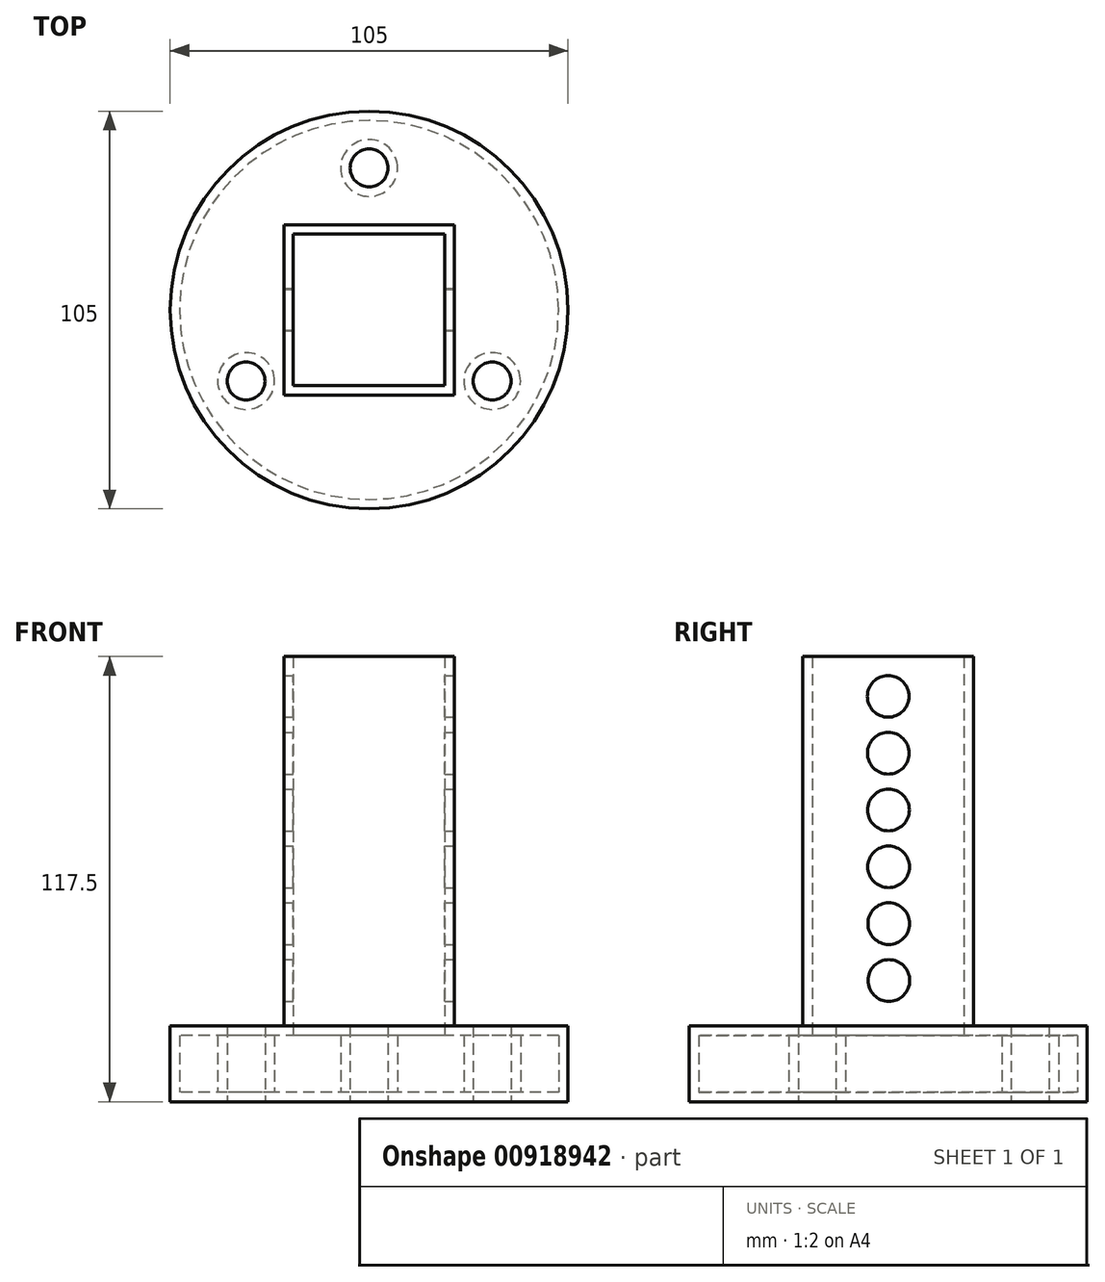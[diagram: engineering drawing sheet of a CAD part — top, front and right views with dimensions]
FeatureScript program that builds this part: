
annotation { "Feature Type Name" : "Feature", "Feature Type Description" : "" }
export const myFeature = defineFeature(function(context is Context, id is Id, definition is map)
    precondition{}
    {
        {
            var Q0;
            Q0=qCreatedBy(makeId("Top.planeOp"),FACE);
            var sketch = newSketch(context, id + "F0", { "sketchPlane" : qUnion([Q0])});
            skCircle(sketch, "E0", {"center": v(0, 0) * mm, "radius": 50 * mm});
            skCircle(sketch, "E1", {"center": v(0, 37.5) * mm, "radius": 7.5 * mm});
            skCircle(sketch, "E2.1.0", {"center": v(-32.48, -18.75) * mm, "radius": 7.5 * mm});
            skCircle(sketch, "E2.2.0", {"center": v(32.48, -18.75) * mm, "radius": 7.5 * mm});
            skSolve(sketch);
        }
        {
            var Q0;
            Q0=makeQuery(id+"F0.imprint","IMPRINT",FACE,{"disambiguationData":[TD([[makeQuery(id+"F0.imprint","IMPRINT",EDGE,{"derivedFrom":sQuery(id+"F0.wireOp",EDGE,"E0")}),1.0]])]});
            extrude(context, id + "F1", {"entities" : qUnion([Q0]), "depth" : 15 * mm, "offsetDistance" : 25 * mm});
        }
        {
            var Q0;
            Q0=makeQuery(id+"F1.opExtrude","CAP_FACE",FACE,{"disambiguationData":[OSD([sQuery(id+"F0.wireOp",EDGE,"E0"),sQuery(id+"F0.wireOp",EDGE,"E1"),sQuery(id+"F0.wireOp",EDGE,"E2.1.0"),sQuery(id+"F0.wireOp",EDGE,"E2.2.0")])],"isStart":false});
            var sketch = newSketch(context, id + "F2", { "sketchPlane" : qUnion([Q0])});
            skLineSegment(sketch, "E3.bottom", {"start": v(20, 20) * mm, "end": v(-20, 20) * mm});
            skLineSegment(sketch, "E3.top", {"start": v(20, -20) * mm, "end": v(-20, -20) * mm});
            skLineSegment(sketch, "E3.left", {"start": v(20, 20) * mm, "end": v(20, -20) * mm});
            skLineSegment(sketch, "E3.right", {"start": v(-20, 20) * mm, "end": v(-20, -20) * mm});
            skPoint(sketch, "E3.middle", {"position": v(0, 0) * mm});
            skSolve(sketch);
        }
        {
            var Q0;
            Q0=makeQuery(id+"F2.imprint","IMPRINT",FACE,{"disambiguationData":[TD([[makeQuery(id+"F2.imprint","IMPRINT",EDGE,{"derivedFrom":sQuery(id+"F2.wireOp",EDGE,"E3.bottom")}),1.0]])]});
            extrude(context, id + "F3", {"entities" : qUnion([Q0]), "operationType" : NewBodyOperationType.ADD, "depth" : 100 * mm, "offsetDistance" : 25 * mm});
        }
        {
            var Q0;
            Q0=makeQuery(id+"F3.opExtrude","CAP_FACE",FACE,{"disambiguationData":[OSD([sQuery(id+"F2.wireOp",EDGE,"E3.bottom"),sQuery(id+"F2.wireOp",EDGE,"E3.top"),sQuery(id+"F2.wireOp",EDGE,"E3.left"),sQuery(id+"F2.wireOp",EDGE,"E3.right")])],"isStart":false});
            shell(context, id + "F4", {"entities" : qUnion([Q0]), "thickness" : 2.5 * mm, "oppositeDirection" : true});
        }
        {
            var Q0;
            Q0=makeQuery(id+"F3.opExtrude","SWEPT_FACE",FACE,{"disambiguationData":[OSD([sQuery(id+"F2.wireOp",EDGE,"E3.left")])]});
            var sketch = newSketch(context, id + "F5", { "sketchPlane" : qUnion([Q0])});
            skCircle(sketch, "E4", {"center": v(0, 104.5) * mm, "radius": 5.5 * mm});
            skCircle(sketch, "E5.1.0.0", {"center": v(0.04, 89.5) * mm, "radius": 5.5 * mm});
            skCircle(sketch, "E5.2.0.0", {"center": v(0.08, 74.5) * mm, "radius": 5.5 * mm});
            skLineSegment(sketch, "E5.direction1", {"start": v(0, 104.5) * mm, "end": v(0.04, 89.5) * mm, "construction": true});
            skLineSegment(sketch, "E5.direction2", {"start": v(0, 104.5) * mm, "end": v(0, 104.6) * mm, "construction": true});
            skCircle(sketch, "E6.0.3.0", {"center": v(0.11, 59.5) * mm, "radius": 5.5 * mm});
            skCircle(sketch, "E6.0.4.0", {"center": v(0.15, 44.5) * mm, "radius": 5.5 * mm});
            skCircle(sketch, "E6.0.5.0", {"center": v(0.19, 29.5) * mm, "radius": 5.5 * mm});
            skSolve(sketch);
        }
        {
            var Q0;
            Q0=makeQuery(id+"F5.imprint","IMPRINT",FACE,{"disambiguationData":[TD([[makeQuery(id+"F5.imprint","IMPRINT",EDGE,{"derivedFrom":sQuery(id+"F5.wireOp",EDGE,"E4")}),1.0]])]});
            var Q1;
            Q1=makeQuery(id+"F5.imprint","IMPRINT",FACE,{"disambiguationData":[TD([[makeQuery(id+"F5.imprint","IMPRINT",EDGE,{"derivedFrom":sQuery(id+"F5.wireOp",EDGE,"E5.1.0.0")}),1.0]])]});
            var Q2;
            Q2=makeQuery(id+"F5.imprint","IMPRINT",FACE,{"disambiguationData":[TD([[makeQuery(id+"F5.imprint","IMPRINT",EDGE,{"derivedFrom":sQuery(id+"F5.wireOp",EDGE,"E5.2.0.0")}),1.0]])]});
            var Q3;
            Q3=makeQuery(id+"F5.imprint","IMPRINT",FACE,{"disambiguationData":[TD([[makeQuery(id+"F5.imprint","IMPRINT",EDGE,{"derivedFrom":sQuery(id+"F5.wireOp",EDGE,"E6.0.3.0")}),1.0]])]});
            var Q4;
            Q4=makeQuery(id+"F5.imprint","IMPRINT",FACE,{"disambiguationData":[TD([[makeQuery(id+"F5.imprint","IMPRINT",EDGE,{"derivedFrom":sQuery(id+"F5.wireOp",EDGE,"E6.0.4.0")}),1.0]])]});
            var Q5;
            Q5=makeQuery(id+"F5.imprint","IMPRINT",FACE,{"disambiguationData":[TD([[makeQuery(id+"F5.imprint","IMPRINT",EDGE,{"derivedFrom":sQuery(id+"F5.wireOp",EDGE,"E6.0.5.0")}),1.0]])]});
            var Q6;
            Q6=makeQuery(id+"F3.opExtrude","SWEPT_FACE",FACE,{"disambiguationData":[OSD([sQuery(id+"F2.wireOp",EDGE,"E3.right")])]});
            extrude(context, id + "F6", {"entities" : qUnion([Q0, Q1, Q2, Q3, Q4, Q5]), "operationType" : NewBodyOperationType.REMOVE, "endBound" : BoundingType.UP_TO_SURFACE, "oppositeDirection" : true, "depth" : 25 * mm, "endBoundEntityFace" : qUnion([Q6]), "offsetDistance" : 25 * mm});
        }
    });
